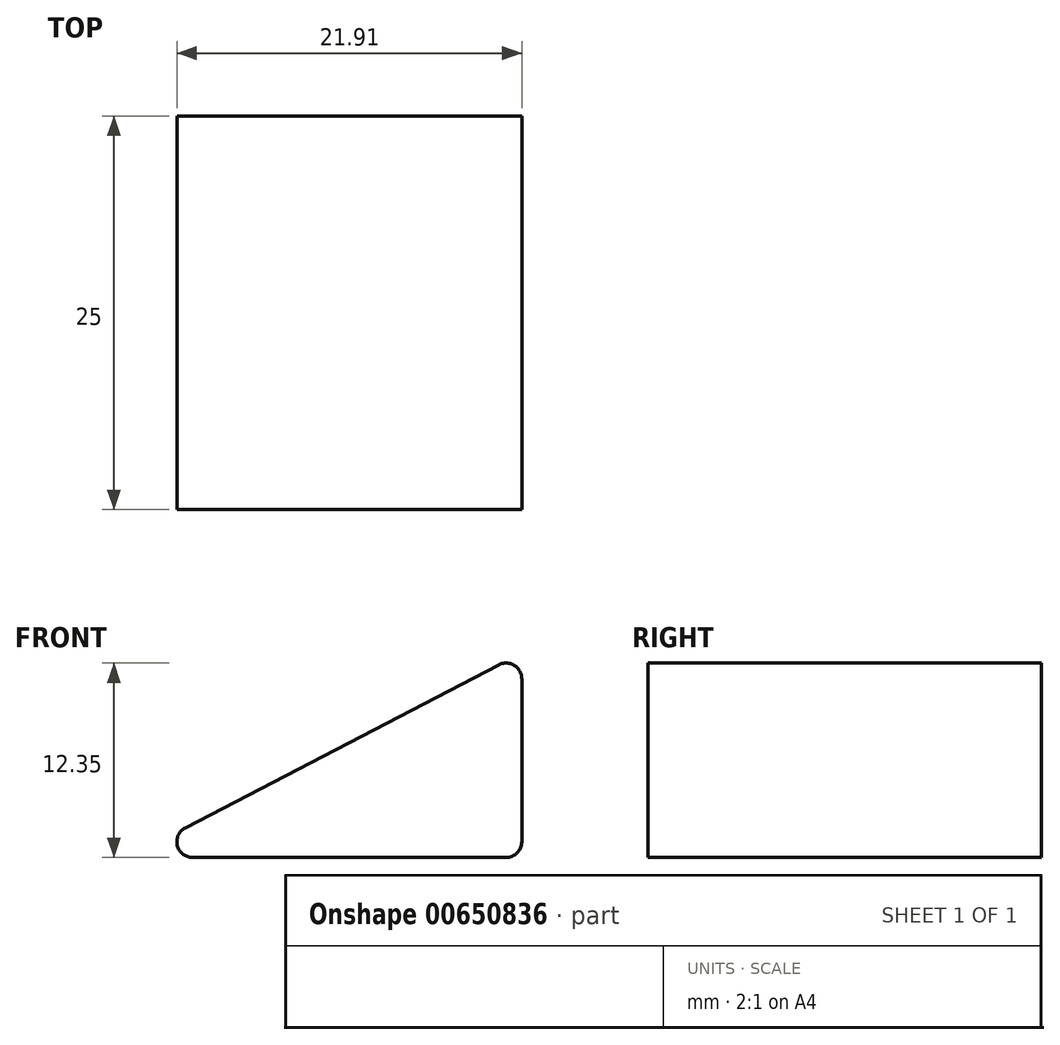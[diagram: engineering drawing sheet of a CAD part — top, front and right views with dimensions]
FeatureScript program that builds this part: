
annotation { "Feature Type Name" : "Feature", "Feature Type Description" : "" }
export const myFeature = defineFeature(function(context is Context, id is Id, definition is map)
    precondition{}
    {
        {
            var Q0;
            Q0=qCreatedBy(makeId("Front.planeOp"),FACE);
            var sketch = newSketch(context, id + "F0", { "sketchPlane" : qUnion([Q0])});
            skLineSegment(sketch, "E0", {"start": v(0, 0) * mm, "end": v(25, 0) * mm});
            skLineSegment(sketch, "E1", {"start": v(25, 0) * mm, "end": v(25, 13) * mm});
            skLineSegment(sketch, "E2", {"start": v(25, 13) * mm, "end": v(0, 0) * mm});
            skSolve(sketch);
        }
        {
            var Q0;
            Q0 = qSketchRegion(id + "F0", true);
            extrude(context, id + "F1", {"entities" : qUnion([Q0]), "depth" : 25 * mm, "offsetDistance" : 25 * mm});
        }
        {
            var Q0;
            Q0=makeQuery(id+"F1.opExtrude","SWEPT_EDGE",EDGE,{"disambiguationData":[OSD([sQuery(id+"F0.wireOp",EDGE,"E1"),sQuery(id+"F0.wireOp",EDGE,"E2")])]});
            var Q1;
            Q1=makeQuery(id+"F1.opExtrude","SWEPT_EDGE",EDGE,{"disambiguationData":[OSD([sQuery(id+"F0.wireOp",EDGE,"E0"),sQuery(id+"F0.wireOp",EDGE,"E1")])]});
            var Q2;
            Q2=makeQuery(id+"F1.opExtrude","SWEPT_EDGE",EDGE,{"disambiguationData":[OSD([sQuery(id+"F0.wireOp",EDGE,"E0"),sQuery(id+"F0.wireOp",EDGE,"E2")])]});
            fillet(context, id + "F2", {"entities" : qUnion([Q0, Q1, Q2]), "radius" : 1 * mm, "tangentPropagation" : true, "allowEdgeOverflow" : false});
        }
    });
